# Revit family: IS_Multisuite_J3291_BIM_ES
name_source: partatom
category: Plumbing Fixtures
units: mm (PartAtom-declared; Revit-internal decimal feet)

## family parameters
Always vertical = No
Cut with Voids When Loaded = No
OmniClass Number = 23.45.05.14
OmniClass Title = Plumbing Fixtures - Sanitary Washing Units
Part Type = Normal
Room Calculation Point = No
Round Connector Dimension = Use Diameter
Shared = No
Work Plane-Based = No

## types (2) — shared parameters
Accesorios = https://www.idealstandard.es
AlturaNominal = 75 mm
AnchuraNominal = 202 mm
Autor = Ideal Standard Iberia
Ayuda = https://www.idealstandard.es
DescripciónUniclass2015 = Bidets
Destacado = 0
Dimensiones = 75 x 140 - 527 x 202 mm
Espacio = Interno
FechaDeCreación = 18/09/2020
GarantíaDeLasPiezas = 2
GarantíaPiezas = 2
GuíaDeInstallación = https://www.idealstandard.es
IfcExportaComo = IfcFurnitureType
InformaciónDeProducto = https://www.idealstandard.es
Installation instructions = https://www.idealstandard.es
Maneta = No
Manufacturer = https://www.idealstandard.es
Marca = Ideal Standard
Nombre = Bidets_MULTI SUITES - FINISHED PRODUCTS_J3291_IdealStandard
NombreDeObjetoBim = IS_IdealStandard_Bidets_MULTI SUITES - FINISHED PRODUCTS_J3291
NúmeroDeModelo = J3291AA
PesoNeto = 1.9
PlatoDeDucha = No
Product group = Wash basins wastes
Referencia = J3291AA
ReferenciaDeModelo = 0
ReferenciaUniclass2015 = Pr_40_20_06_11
Repuestos = https://www.idealstandard.es
Revisión = 1
Teléfono = +34 93 561 80 00
TipoDeExportaciónIfc = BIDET
TipoDeGarantía = Garantía del Fabricante
URL = https://www.idealstandard.es
Uniclass 2015 Code = Pr_70_55_96_97
Uniclass 2015 Name = Wash basins wastes
UnidadDeTiempo = año
UnidadDeVolúmen = Litros
UnidadDeÁrea = milímetros
UnidadGarantía = año
UnidadLineal = milímetros
UnidadMonetaria = €
UrlDelFabricante = https://www.idealstandard.es
Versión = 1
VersiónUniclass2015 = v1.1
ÁreaDeMedición = Interna
zero-valued in all types: Cost, DiámetroDeDesagüe, GrosorDelMaterial, LongitudNominal, NivelDeDesbordamiento, PesoBruto, ProfundidadNominal

## per-type parameters (varying)
| type | Acabado | CódigoDeBarras | Description | MAT | Model |
| J3291AA - FREEFLOW 1 1/4 METAL DOMED WASTE UNSLOTTEDLOTTED  - CHROME | cromo | 8023246201941 | freeflow 1 1/4 mtl abovedado wst sin ranuras - cromo | ChromePolished AA | J3291AA |
| J3291XG - FREEFLOW 1 1/4 METAL DOMED WASTE UNSLOTTEDLOTTED  - SILK BLACK | negroseda | 3800861101666 | freeflow 1 1/4 mtl abovedado wst sin ranuras - negro seda | Silk_Black_XG | J3291XG |

## geometry (parser evidence)
native form markers: Sweep x3
no freeform markers — native parametric forms only
